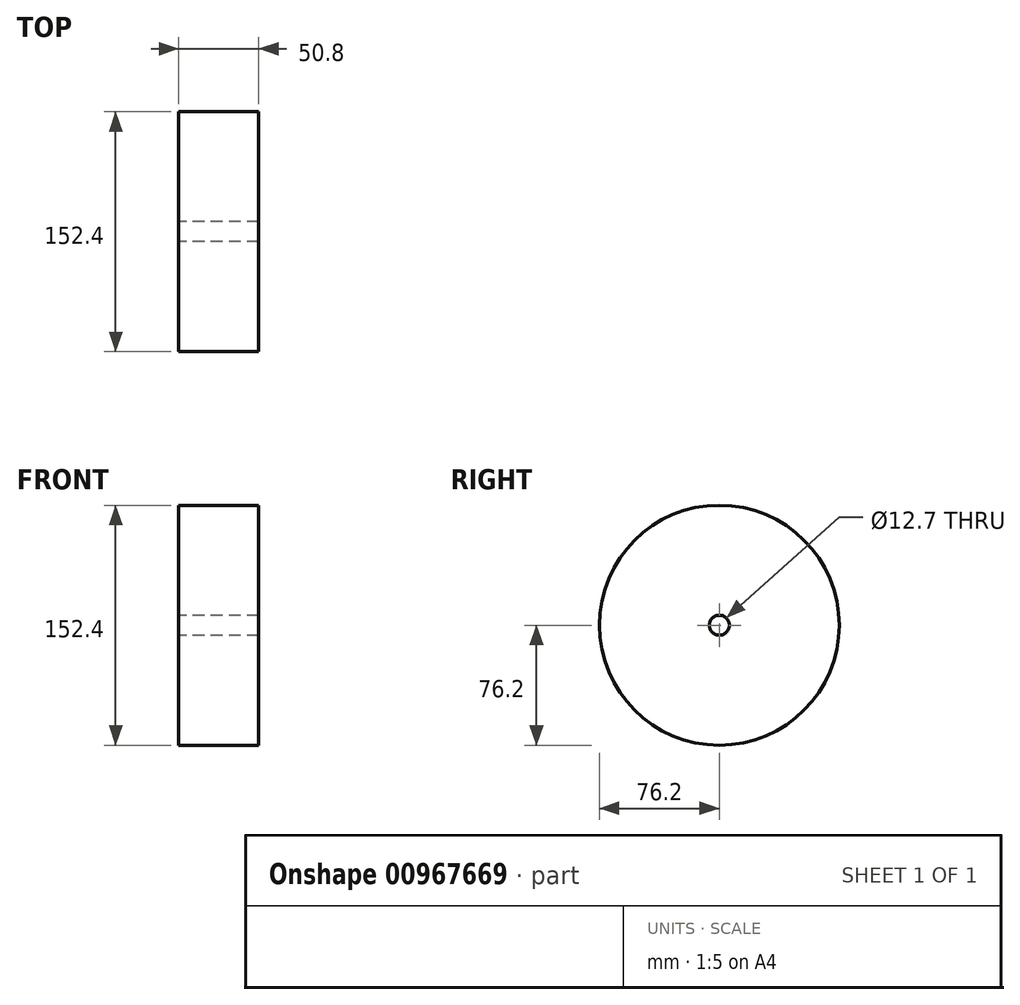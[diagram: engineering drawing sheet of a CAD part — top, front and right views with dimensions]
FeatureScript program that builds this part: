
annotation { "Feature Type Name" : "Feature", "Feature Type Description" : "" }
export const myFeature = defineFeature(function(context is Context, id is Id, definition is map)
    precondition{}
    {
        {
            var Q0;
            Q0=qCreatedBy(makeId("Right.planeOp"),FACE);
            var sketch = newSketch(context, id + "F0", { "sketchPlane" : qUnion([Q0])});
            skCircle(sketch, "E0", {"center": v(0, 0) * mm, "radius": 76.2 * mm});
            skCircle(sketch, "E1", {"center": v(0, 0) * mm, "radius": 6.35 * mm});
            skSolve(sketch);
        }
        {
            var Q0;
            Q0 = qSketchRegion(id + "F0", true);
            extrude(context, id + "F1", {"entities" : qUnion([Q0]), "depth" : 50.8 * mm, "offsetDistance" : 25.4 * mm});
        }
    });
